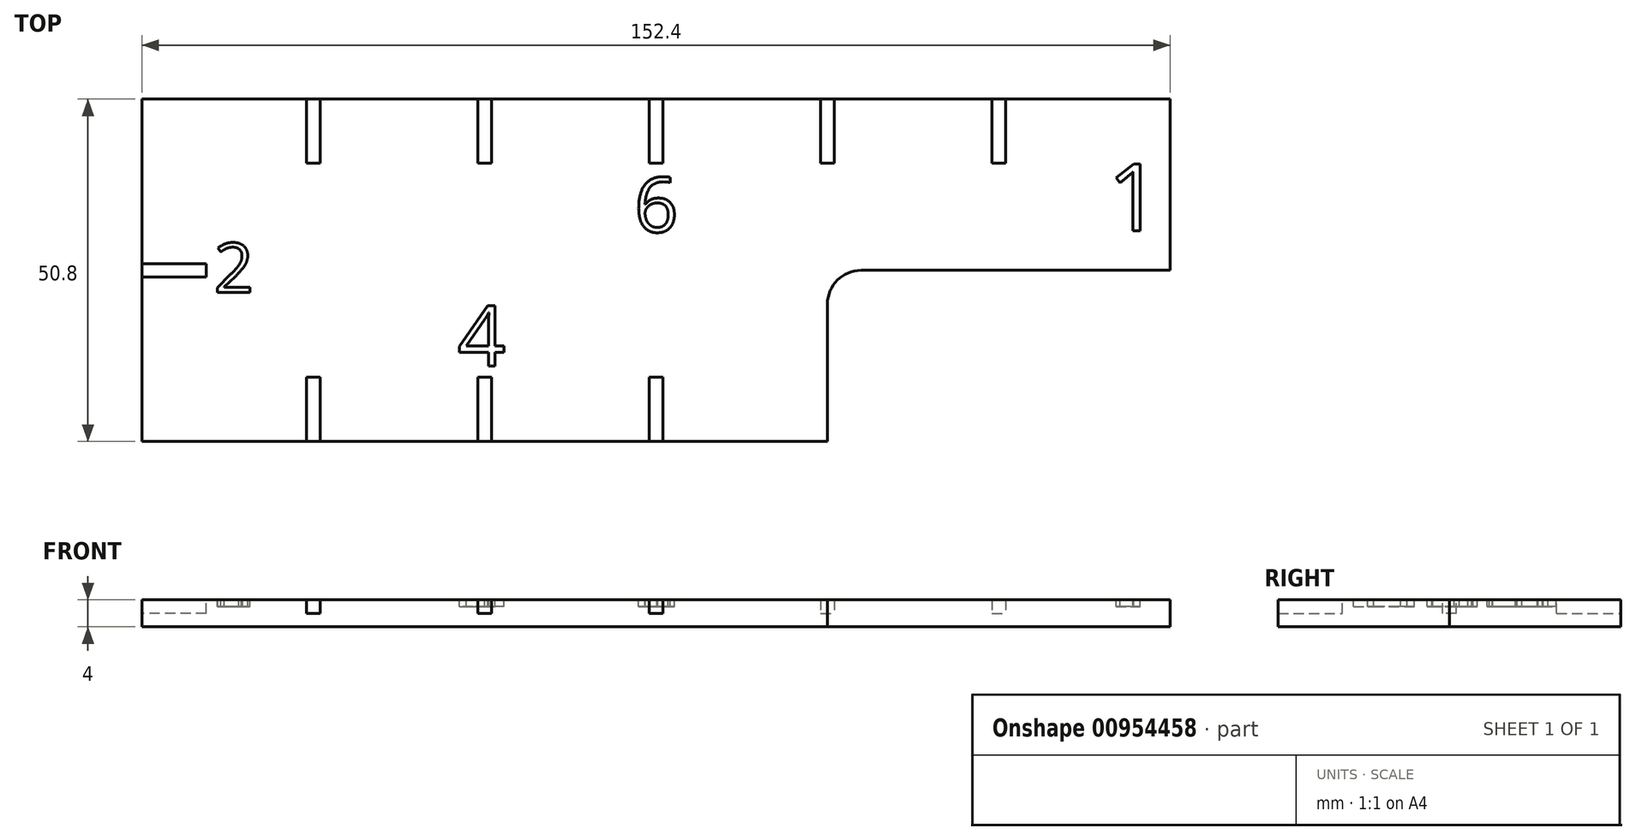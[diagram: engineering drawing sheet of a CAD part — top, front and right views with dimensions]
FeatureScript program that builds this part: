
annotation { "Feature Type Name" : "Feature", "Feature Type Description" : "" }
export const myFeature = defineFeature(function(context is Context, id is Id, definition is map)
    precondition{}
    {
        {
            var Q0;
            Q0=qCreatedBy(makeId("Top.planeOp"),FACE);
            var sketch = newSketch(context, id + "F0", { "sketchPlane" : qUnion([Q0])});
            skLineSegment(sketch, "E0.bottom", {"start": v(-50.8, 25.4) * mm, "end": v(50.8, 25.4) * mm});
            skLineSegment(sketch, "E0.top", {"start": v(-50.8, -25.4) * mm, "end": v(50.8, -25.4) * mm});
            skLineSegment(sketch, "E0.left", {"start": v(-50.8, 25.4) * mm, "end": v(-50.8, -25.4) * mm});
            skPoint(sketch, "E0.middle", {"position": v(0, 0) * mm});
            skLineSegment(sketch, "E1.bottom", {"start": v(50.8, 25.4) * mm, "end": v(101.6, 25.4) * mm});
            skLineSegment(sketch, "E1.top", {"start": v(55.8, 0) * mm, "end": v(101.6, 0) * mm});
            skLineSegment(sketch, "E1.right", {"start": v(101.6, 25.4) * mm, "end": v(101.6, 0) * mm});
            skLineSegment(sketch, "E2", {"start": v(50.8, -25.4) * mm, "end": v(50.8, -5) * mm});
            skPoint(sketch, "E3.visualSharp", {"position": v(50.8, 0) * mm});
            skArc(sketch, "E3.filletArc", {"start": v(55.8, 0) * mm, "mid": v(52.26, -1.46) * mm, "end": v(50.8, -5) * mm});
            skSolve(sketch);
        }
        {
            var Q0;
            Q0 = qSketchRegion(id + "F0", true);
            extrude(context, id + "F1", {"entities" : qUnion([Q0]), "depth" : 4 * mm, "offsetDistance" : 25 * mm});
        }
        {
            var Q0;
            Q0=makeQuery(id+"F1.opExtrude","CAP_FACE",FACE,{"disambiguationData":[OSD([sQuery(id+"F0.wireOp",EDGE,"E0.bottom"),sQuery(id+"F0.wireOp",EDGE,"E0.top"),sQuery(id+"F0.wireOp",EDGE,"E0.left"),sQuery(id+"F0.wireOp",EDGE,"E1.bottom"),sQuery(id+"F0.wireOp",EDGE,"E1.top"),sQuery(id+"F0.wireOp",EDGE,"E1.right"),sQuery(id+"F0.wireOp",EDGE,"E2"),sQuery(id+"F0.wireOp",EDGE,"E3.filletArc")])],"isStart":false});
            var sketch = newSketch(context, id + "F2", { "sketchPlane" : qUnion([Q0])});
            skLineSegment(sketch, "E4", {"start": v(-50.8, 25.4) * mm, "end": v(-25.4, 25.4) * mm});
            skLineSegment(sketch, "E5.bottom", {"start": v(-24.4, 15.88) * mm, "end": v(-26.4, 15.88) * mm});
            skLineSegment(sketch, "E5.top", {"start": v(-24.4, 34.92) * mm, "end": v(-26.4, 34.92) * mm});
            skLineSegment(sketch, "E5.left", {"start": v(-24.4, 15.88) * mm, "end": v(-24.4, 34.92) * mm});
            skLineSegment(sketch, "E5.right", {"start": v(-26.4, 15.88) * mm, "end": v(-26.4, 34.92) * mm});
            skPoint(sketch, "E5.middle", {"position": v(-25.4, 25.4) * mm});
            skLineSegment(sketch, "E6", {"start": v(-24.4, 25.4) * mm, "end": v(0, 25.4) * mm});
            skLineSegment(sketch, "E7.bottom", {"start": v(1, 15.87) * mm, "end": v(-1, 15.87) * mm});
            skLineSegment(sketch, "E7.top", {"start": v(1, 34.92) * mm, "end": v(-1, 34.92) * mm});
            skLineSegment(sketch, "E7.left", {"start": v(1, 15.87) * mm, "end": v(1, 34.92) * mm});
            skLineSegment(sketch, "E7.right", {"start": v(-1, 15.87) * mm, "end": v(-1, 34.92) * mm});
            skPoint(sketch, "E7.middle", {"position": v(0, 25.4) * mm});
            skLineSegment(sketch, "E8", {"start": v(2, 25.4) * mm, "end": v(25.4, 25.4) * mm});
            skLineSegment(sketch, "E9.bottom", {"start": v(26.4, 15.87) * mm, "end": v(24.4, 15.87) * mm});
            skLineSegment(sketch, "E9.top", {"start": v(26.4, 34.92) * mm, "end": v(24.4, 34.92) * mm});
            skLineSegment(sketch, "E9.left", {"start": v(26.4, 15.87) * mm, "end": v(26.4, 34.92) * mm});
            skLineSegment(sketch, "E9.right", {"start": v(24.4, 15.87) * mm, "end": v(24.4, 34.92) * mm});
            skPoint(sketch, "E9.middle", {"position": v(25.4, 25.4) * mm});
            skLineSegment(sketch, "E10", {"start": v(28.4, 25.4) * mm, "end": v(50.8, 25.4) * mm});
            skLineSegment(sketch, "E11.bottom", {"start": v(51.8, 15.87) * mm, "end": v(49.8, 15.87) * mm});
            skLineSegment(sketch, "E11.top", {"start": v(51.8, 34.92) * mm, "end": v(49.8, 34.92) * mm});
            skLineSegment(sketch, "E11.left", {"start": v(51.8, 15.87) * mm, "end": v(51.8, 34.92) * mm});
            skLineSegment(sketch, "E11.right", {"start": v(49.8, 15.87) * mm, "end": v(49.8, 34.92) * mm});
            skPoint(sketch, "E11.middle", {"position": v(50.8, 25.4) * mm});
            skLineSegment(sketch, "E12", {"start": v(51.8, 25.4) * mm, "end": v(76.2, 25.4) * mm});
            skLineSegment(sketch, "E13.bottom", {"start": v(77.2, 15.87) * mm, "end": v(75.2, 15.87) * mm});
            skLineSegment(sketch, "E13.top", {"start": v(77.2, 34.92) * mm, "end": v(75.2, 34.92) * mm});
            skLineSegment(sketch, "E13.left", {"start": v(77.2, 15.87) * mm, "end": v(77.2, 34.92) * mm});
            skLineSegment(sketch, "E13.right", {"start": v(75.2, 15.87) * mm, "end": v(75.2, 34.92) * mm});
            skPoint(sketch, "E13.middle", {"position": v(76.2, 25.4) * mm});
            skLineSegment(sketch, "E14", {"start": v(-50.8, -25.4) * mm, "end": v(-50.8, 0) * mm});
            skLineSegment(sketch, "E15.bottom", {"start": v(-41.27, 1) * mm, "end": v(-41.27, -1) * mm});
            skLineSegment(sketch, "E15.top", {"start": v(-60.32, 1) * mm, "end": v(-60.32, -1) * mm});
            skLineSegment(sketch, "E15.left", {"start": v(-41.27, 1) * mm, "end": v(-60.32, 1) * mm});
            skLineSegment(sketch, "E15.right", {"start": v(-41.27, -1) * mm, "end": v(-60.32, -1) * mm});
            skPoint(sketch, "E15.middle", {"position": v(-50.8, 0) * mm});
            skLineSegment(sketch, "E16", {"start": v(-50.8, -25.4) * mm, "end": v(-25.4, -25.4) * mm});
            skLineSegment(sketch, "E17.bottom", {"start": v(-24.4, -34.93) * mm, "end": v(-26.4, -34.93) * mm});
            skLineSegment(sketch, "E17.top", {"start": v(-24.4, -15.88) * mm, "end": v(-26.4, -15.88) * mm});
            skLineSegment(sketch, "E17.left", {"start": v(-24.4, -34.93) * mm, "end": v(-24.4, -15.88) * mm});
            skLineSegment(sketch, "E17.right", {"start": v(-26.4, -34.93) * mm, "end": v(-26.4, -15.88) * mm});
            skPoint(sketch, "E17.middle", {"position": v(-25.4, -25.4) * mm});
            skLineSegment(sketch, "E18", {"start": v(-24.4, -25.4) * mm, "end": v(0, -25.4) * mm});
            skLineSegment(sketch, "E19.bottom", {"start": v(1, -34.93) * mm, "end": v(-1, -34.93) * mm});
            skLineSegment(sketch, "E19.top", {"start": v(1, -15.88) * mm, "end": v(-1, -15.88) * mm});
            skLineSegment(sketch, "E19.left", {"start": v(1, -34.93) * mm, "end": v(1, -15.88) * mm});
            skLineSegment(sketch, "E19.right", {"start": v(-1, -34.93) * mm, "end": v(-1, -15.88) * mm});
            skPoint(sketch, "E19.middle", {"position": v(0, -25.4) * mm});
            skLineSegment(sketch, "E20", {"start": v(2, -25.4) * mm, "end": v(25.4, -25.4) * mm});
            skLineSegment(sketch, "E21.bottom", {"start": v(26.4, -34.92) * mm, "end": v(24.4, -34.92) * mm});
            skLineSegment(sketch, "E21.top", {"start": v(26.4, -15.88) * mm, "end": v(24.4, -15.88) * mm});
            skLineSegment(sketch, "E21.left", {"start": v(26.4, -34.93) * mm, "end": v(26.4, -15.88) * mm});
            skLineSegment(sketch, "E21.right", {"start": v(24.4, -34.92) * mm, "end": v(24.4, -15.88) * mm});
            skPoint(sketch, "E21.middle", {"position": v(25.4, -25.4) * mm});
            skSolve(sketch);
        }
        {
            var Q0;
            Q0 = qSketchRegion(id + "F2", true);
            extrude(context, id + "F3", {"entities" : qUnion([Q0]), "operationType" : NewBodyOperationType.REMOVE, "oppositeDirection" : true, "depth" : 2 * mm, "offsetDistance" : 25 * mm});
        }
        {
            var Q0;
            Q0=makeQuery(id+"F1.opExtrude","CAP_FACE",FACE,{"disambiguationData":[OSD([sQuery(id+"F0.wireOp",EDGE,"E0.bottom"),sQuery(id+"F0.wireOp",EDGE,"E0.top"),sQuery(id+"F0.wireOp",EDGE,"E0.left"),sQuery(id+"F0.wireOp",EDGE,"E1.bottom"),sQuery(id+"F0.wireOp",EDGE,"E1.top"),sQuery(id+"F0.wireOp",EDGE,"E1.right"),sQuery(id+"F0.wireOp",EDGE,"E2"),sQuery(id+"F0.wireOp",EDGE,"E3.filletArc")])],"isStart":false});
            var sketch = newSketch(context, id + "F4", { "sketchPlane" : qUnion([Q0])});
            skText(sketch, "E22", { "text": "2", "fontName": "OpenSans-Regular.ttf"});
            skText(sketch, "E23", { "text": "6", "fontName": "OpenSans-Regular.ttf"});
            skText(sketch, "E24", { "text": "4", "fontName": "OpenSans-Regular.ttf"});
            skText(sketch, "E25", { "text": "1", "fontName": "OpenSans-Regular.ttf"});
            const initialGuessF4  = {"E22": [-0.04013, -0.00329, 1, 0, 0.00739], "E23": [0.02218, 0.00568, 1, 0, 0.00817], "E24": [-0.00404, -0.0142, 1, 0, 0.009], "E25": [0.0923, 0.00588, 1, 0, 0.01]};
            skSetInitialGuess(sketch, initialGuessF4);
            skSolve(sketch);
        }
        {
            var Q0;
            Q0 = qSketchRegion(id + "F4", true);
            extrude(context, id + "F5", {"entities" : qUnion([Q0]), "operationType" : NewBodyOperationType.REMOVE, "oppositeDirection" : true, "depth" : 1 * mm, "offsetDistance" : 25 * mm});
        }
    });
